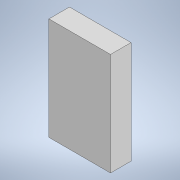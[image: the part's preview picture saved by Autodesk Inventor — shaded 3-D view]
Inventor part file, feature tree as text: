
AUTODESK INVENTOR PART (.ipt)
format: ipt  version: 2021 (Build 250183000, 183)  size: 90,624 bytes
history: native  units: mm
features: other x1, extrude x1, sketch x1
ambient origin geometry x8: Origin, YZ Plane, XZ Plane, XY Plane, X Axis, Y Axis, Z Axis, Center Point
bodies: Body1 (feature_tree)
feature tree (3):
  other  "ソリッド1"
  extrude  "押し出し1"  Depth=1000.0mm
  sketch  "スケッチ1"
